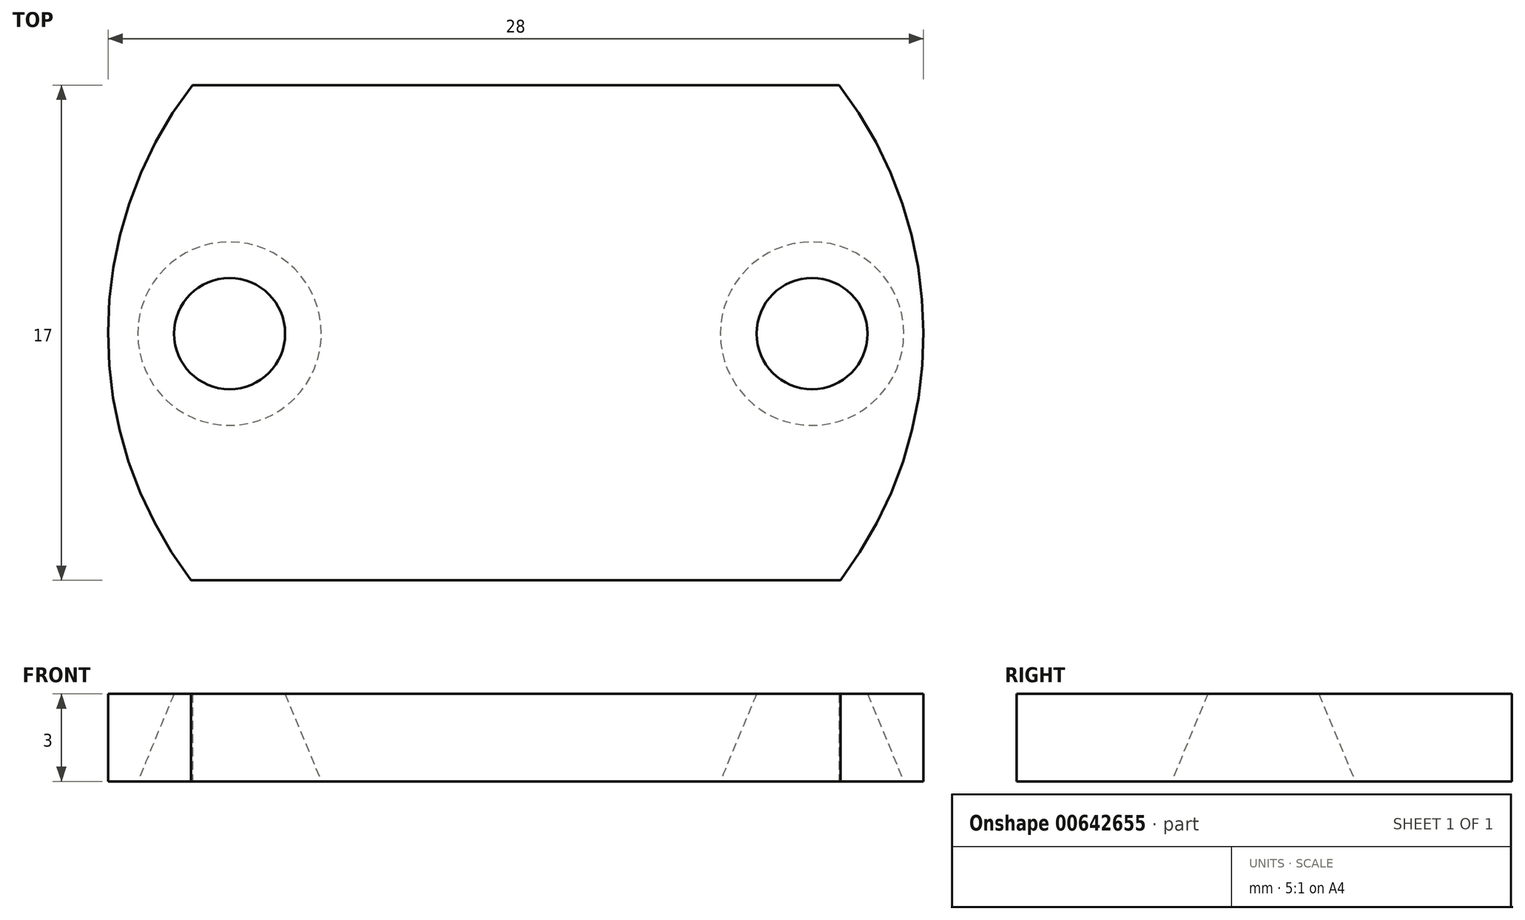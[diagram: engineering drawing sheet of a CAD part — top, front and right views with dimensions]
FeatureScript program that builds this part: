
annotation { "Feature Type Name" : "Feature", "Feature Type Description" : "" }
export const myFeature = defineFeature(function(context is Context, id is Id, definition is map)
    precondition{}
    {
        {
            var Q0;
            Q0=qCreatedBy(makeId("Top.planeOp"),FACE);
            var sketch = newSketch(context, id + "F0", { "sketchPlane" : qUnion([Q0])});
            skArc(sketch, "E0", {"start": v(-11.1, 8.53) * mm, "mid": v(-14, 0.04) * mm, "end": v(-11.15, -8.47) * mm});
            skLineSegment(sketch, "E1", {"start": v(-11.1, 8.53) * mm, "end": v(11.1, 8.53) * mm});
            skLineSegment(sketch, "E2", {"start": v(-11.15, -8.47) * mm, "end": v(11.15, -8.47) * mm});
            skArc(sketch, "E3.trimOffspring", {"start": v(11.15, -8.47) * mm, "mid": v(14, 0.04) * mm, "end": v(11.1, 8.53) * mm});
            skSolve(sketch);
        }
        {
            var Q0;
            Q0 = qSketchRegion(id + "F0", true);
            extrude(context, id + "F1", {"entities" : qUnion([Q0]), "depth" : 3 * mm, "offsetDistance" : 25.4 * mm});
        }
        {
            var Q0;
            Q0=makeQuery(id+"F1.opExtrude","CAP_FACE",FACE,{"disambiguationData":[OSD([sQuery(id+"F0.wireOp",EDGE,"E0"),sQuery(id+"F0.wireOp",EDGE,"E1"),sQuery(id+"F0.wireOp",EDGE,"E2"),sQuery(id+"F0.wireOp",EDGE,"E3.trimOffspring")])],"isStart":true});
            var sketch = newSketch(context, id + "F2", { "sketchPlane" : qUnion([Q0])});
            skPoint(sketch, "E4", {"position": v(-9.83, 0) * mm});
            skPoint(sketch, "E5", {"position": v(10.17, 0) * mm});
            skSolve(sketch);
        }
        {
            var Q0;
            Q0=sQuery(id+"F2.wireOp",VERTEX,"E4");
            var Q1;
            Q1=sQuery(id+"F2.wireOp",VERTEX,"E5");
            var Q2;
            Q2=makeQuery(id+"F1.opExtrude","SWEPT_BODY",BODY,{"disambiguationData":[OSD([sQuery(id+"F0.wireOp",EDGE,"E0"),sQuery(id+"F0.wireOp",EDGE,"E1"),sQuery(id+"F0.wireOp",EDGE,"E2"),sQuery(id+"F0.wireOp",EDGE,"E3.trimOffspring")])]});
            hole(context, id + "F3", {"style" : HoleStyle.C_SINK, "endStyle" : HoleEndStyle.THROUGH, "holeDiameter" : 3.4 * mm, "cSinkDiameter" : 6.3 * mm, "cSinkAngle" : 45 * degree, "majorDiameter" : 6.35 * mm, "isTappedThrough" : true, "tappedDepth" : 12.7 * mm, "tapClearance" : 3, "locations" : qUnion([Q0, Q1]), "scope" : qUnion([Q2])});
        }
    });
